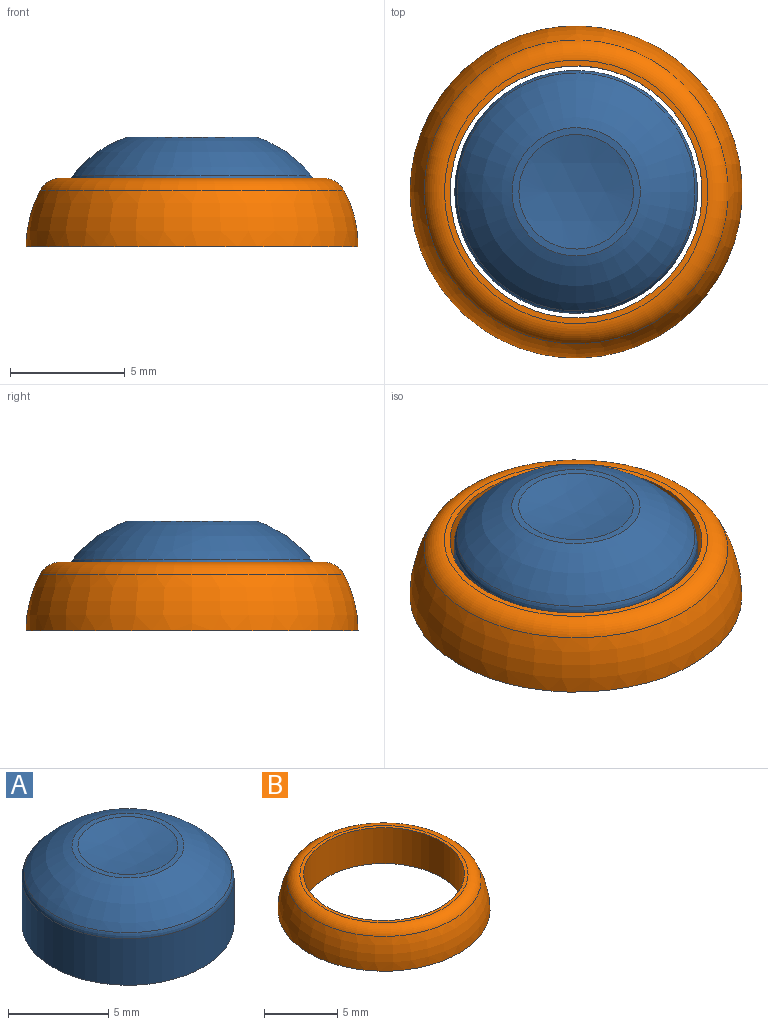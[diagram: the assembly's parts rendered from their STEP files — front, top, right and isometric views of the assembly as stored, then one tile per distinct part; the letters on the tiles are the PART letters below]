
ASSEMBLY  parts=2 mates=1
PART A: 6 faces, bbox 11.5x11.5x5.1 mm
  f0: sphere r=10.57mm, area 19.9mm2, adj f5
  f1: torus R=1.27mm, axis (0,0,-1), area 75.7mm2, adj f2,f5
  f2: torus R=4.8mm, axis (0,0,-1), area 11.1mm2, adj f1,f3
  f3: cylinder r=5.3mm len=10.6mm, axis (0,0,-1), area 94.3mm2, adj f2,f4
  f4: plane 10.6x10.6mm, normal (0,0,-1), area 88.2mm2, adj f3
  f5: plane 5.6x5.6mm, normal (0,0,1), area 5mm2, adj f0,f1
PART B: 5 faces, bbox 14.6x14.6x3 mm
  f0: cylinder r=5.5mm len=11mm, axis (0,0,-1), area 103.7mm2, adj f3,f4
  f1: torus R=5.75mm, axis (0,0,-1), area 42.4mm2, adj f2,f3
  f2: torus R=2mm, axis (0,0,-1), area 113.8mm2, adj f1,f4
  f3: plane 11.5x11.5mm, normal (0,0,1), area 8.8mm2, adj f0,f1
  f4: plane 14.5x14.5mm, normal (0,0,-1), area 70.1mm2, adj f0,f2
PLACE A at identity
PLACE B at identity fixed
MATE fastened B.f0 <-> A.f3  axis (0,0,-1) through (0,0,18)mm
